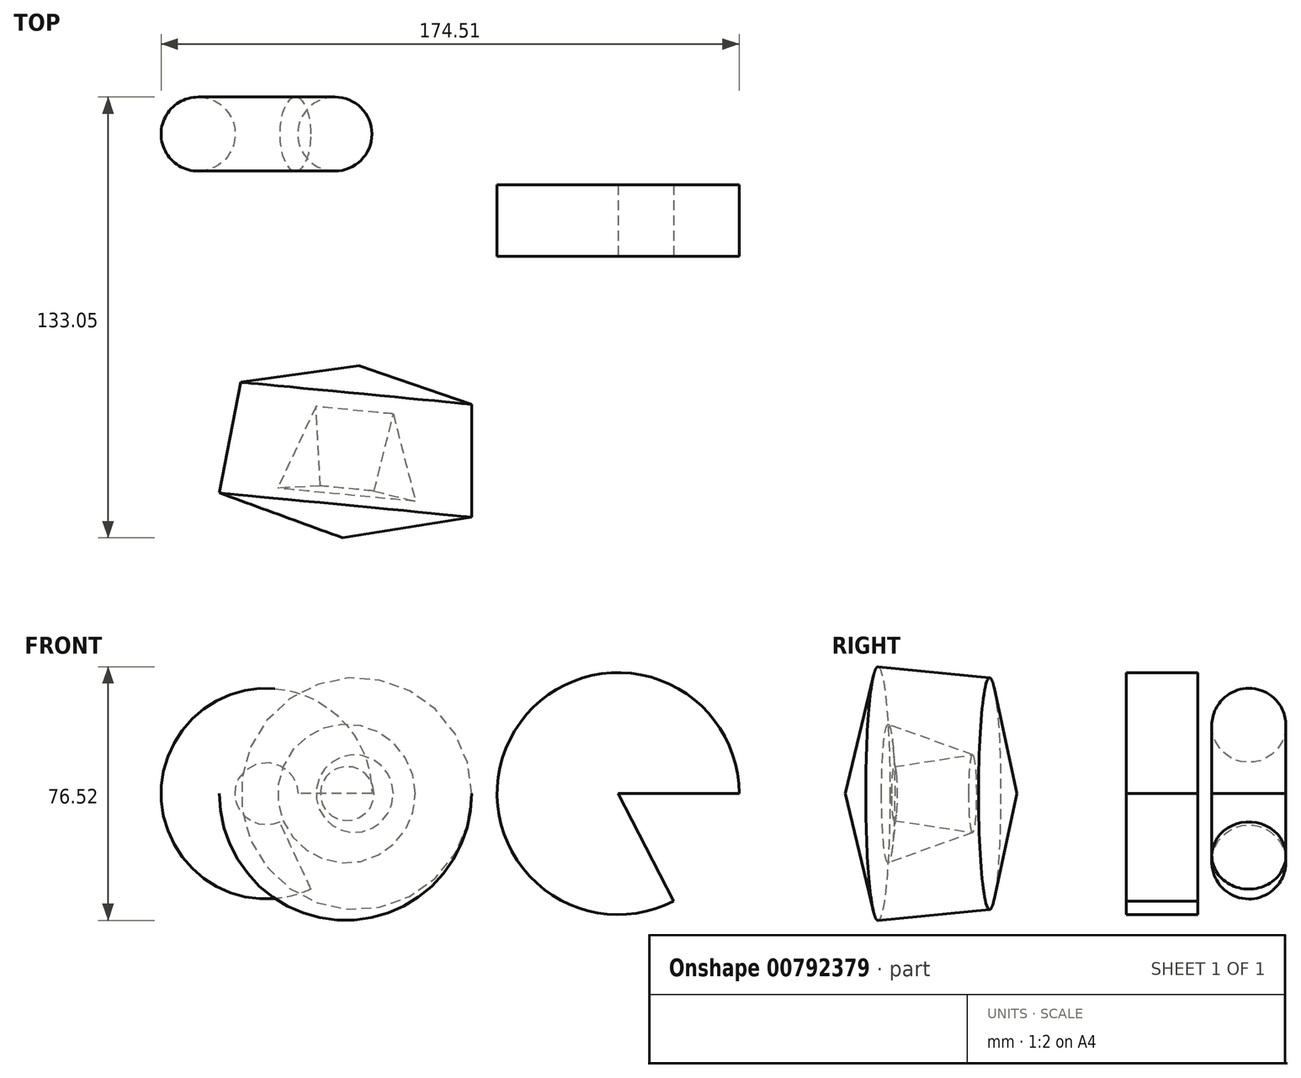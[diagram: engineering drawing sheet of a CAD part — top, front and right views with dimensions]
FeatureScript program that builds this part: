
annotation { "Feature Type Name" : "Feature", "Feature Type Description" : "" }
export const myFeature = defineFeature(function(context is Context, id is Id, definition is map)
    precondition{}
    {
        {
            var Q0;
            Q0=qCreatedBy(makeId("Top.planeOp"),FACE);
            var sketch = newSketch(context, id + "F0", { "sketchPlane" : qUnion([Q0])});
            skCircle(sketch, "E0", {"center": v(-62.28, 52.52) * mm, "radius": 11.18 * mm});
            skLineSegment(sketch, "E1.bottom", {"start": v(23.25, 37.16) * mm, "end": v(59.79, 37.16) * mm});
            skLineSegment(sketch, "E1.top", {"start": v(23.25, 15.57) * mm, "end": v(59.79, 15.57) * mm});
            skLineSegment(sketch, "E1.left", {"start": v(23.25, 37.16) * mm, "end": v(23.25, 15.57) * mm});
            skLineSegment(sketch, "E1.right", {"start": v(59.79, 37.16) * mm, "end": v(59.79, 15.57) * mm});
            skLineSegment(sketch, "E2", {"start": v(-55, -17.45) * mm, "end": v(-20.95, -29.08) * mm});
            skLineSegment(sketch, "E3", {"start": v(-20.95, -29.08) * mm, "end": v(-20.95, -63.13) * mm});
            skLineSegment(sketch, "E4", {"start": v(-20.95, -63.13) * mm, "end": v(-59.98, -69.35) * mm});
            skLineSegment(sketch, "E5", {"start": v(-59.98, -69.35) * mm, "end": v(-55, -17.45) * mm});
            skLineSegment(sketch, "E6", {"start": v(-44.62, -31.99) * mm, "end": v(-50.43, -55.24) * mm});
            skLineSegment(sketch, "E7", {"start": v(-50.43, -55.24) * mm, "end": v(-37.93, -58.36) * mm});
            skLineSegment(sketch, "E8", {"start": v(-37.93, -58.36) * mm, "end": v(-44.62, -31.99) * mm});
            skLineSegment(sketch, "E9", {"start": v(-82.91, 71.7) * mm, "end": v(-82.91, 30.26) * mm, "construction": true});
            skSolve(sketch);
        }
        {
            var Q0;
            Q0=makeQuery(id+"F0.imprint","IMPRINT",FACE,{"disambiguationData":[TD([[makeQuery(id+"F0.imprint","IMPRINT",EDGE,{"derivedFrom":sQuery(id+"F0.wireOp",EDGE,"E1.bottom")}),-1.0]])]});
            var Q1;
            Q1=sQuery(id+"F0.wireOp",EDGE,"E1.left");
            revolve(context, id + "F1", {"surfaceOperationType" : NewSurfaceOperationType.NEW, "entities" : qUnion([Q0]), "axis" : qUnion([Q1]), "revolveType" : RevolveType.ONE_DIRECTION, "angle" : 297.34 * degree});
        }
        {
            var Q0;
            Q0=makeQuery(id+"F0.imprint","IMPRINT",FACE,{"disambiguationData":[TD([[makeQuery(id+"F0.imprint","IMPRINT",EDGE,{"derivedFrom":sQuery(id+"F0.wireOp",EDGE,"E0")}),1.0]])]});
            var Q1;
            Q1=sQuery(id+"F0.wireOp",EDGE,"E9");
            revolve(context, id + "F2", {"surfaceOperationType" : NewSurfaceOperationType.NEW, "entities" : qUnion([Q0]), "axis" : qUnion([Q1]), "revolveType" : RevolveType.ONE_DIRECTION, "angle" : 295 * degree});
        }
        {
            var Q0;
            Q0=makeQuery(id+"F0.imprint","IMPRINT",FACE,{"disambiguationData":[TD([[makeQuery(id+"F0.imprint","IMPRINT",EDGE,{"derivedFrom":sQuery(id+"F0.wireOp",EDGE,"E2")}),-1.0]])]});
            var Q1;
            Q1=sQuery(id+"F0.wireOp",EDGE,"E5");
            revolve(context, id + "F3", {"surfaceOperationType" : NewSurfaceOperationType.NEW, "entities" : qUnion([Q0]), "axis" : qUnion([Q1]), "revolveType" : RevolveType.FULL});
        }
    });
